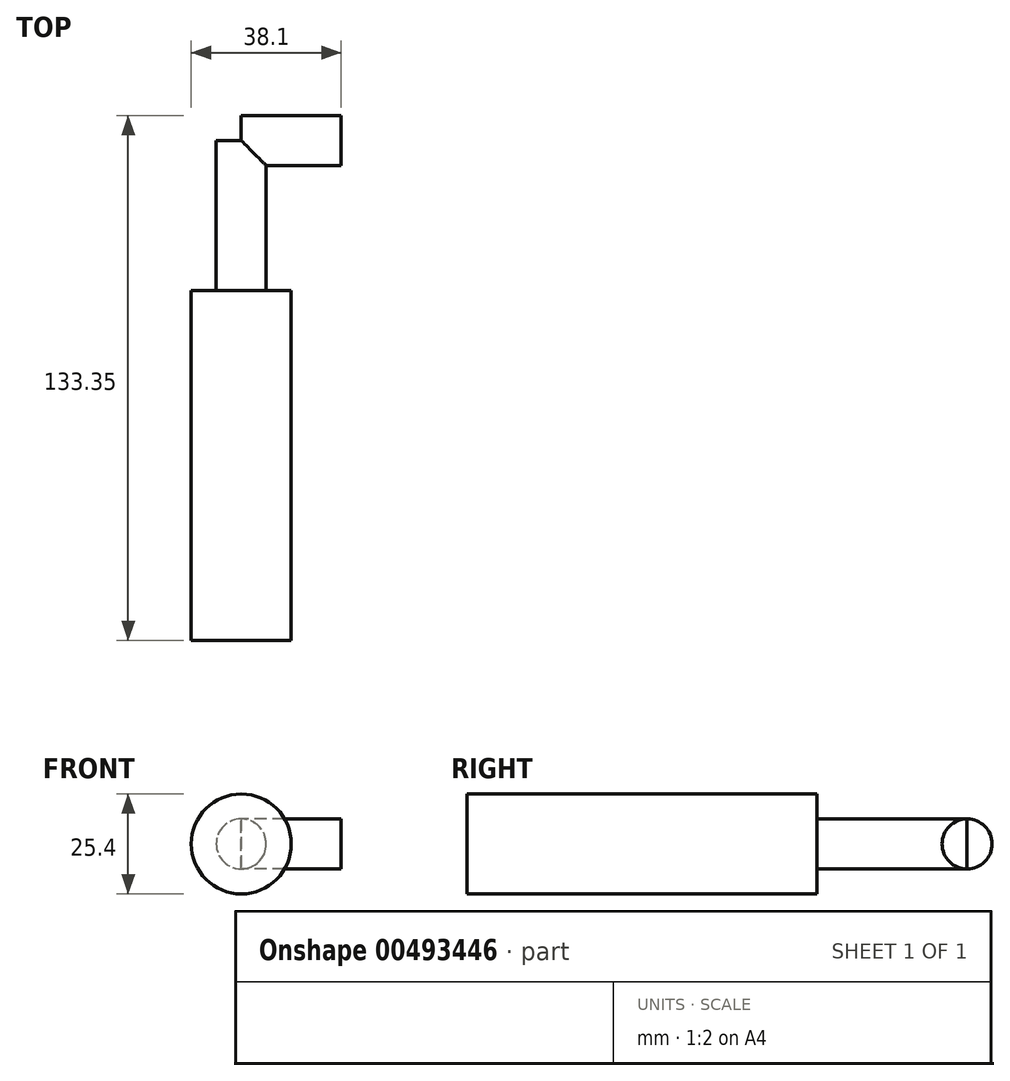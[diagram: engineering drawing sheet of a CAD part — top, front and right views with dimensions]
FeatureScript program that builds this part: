
annotation { "Feature Type Name" : "Feature", "Feature Type Description" : "" }
export const myFeature = defineFeature(function(context is Context, id is Id, definition is map)
    precondition{}
    {
        {
            var Q0;
            Q0=qCreatedBy(makeId("Front.planeOp"),FACE);
            var sketch = newSketch(context, id + "F0", { "sketchPlane" : qUnion([Q0])});
            skCircle(sketch, "E0", {"center": v(0, 0) * mm, "radius": 12.7 * mm});
            skSolve(sketch);
        }
        {
            var Q0;
            Q0=makeQuery(id+"F0.imprint","IMPRINT",FACE,{"disambiguationData":[TD([[makeQuery(id+"F0.imprint","IMPRINT",EDGE,{"derivedFrom":sQuery(id+"F0.wireOp",EDGE,"E0")}),1.0]])]});
            extrude(context, id + "F1", {"entities" : qUnion([Q0]), "oppositeDirection" : true, "depth" : 88.9 * mm});
        }
        {
            var Q0;
            Q0=makeQuery(id+"F1.opExtrude","CAP_FACE",FACE,{"disambiguationData":[OSD([sQuery(id+"F0.wireOp",EDGE,"E0")])],"isStart":false});
            var sketch = newSketch(context, id + "F2", { "sketchPlane" : qUnion([Q0])});
            skCircle(sketch, "E1", {"center": v(0, 0) * mm, "radius": 6.35 * mm});
            skSolve(sketch);
        }
        {
            var Q0;
            Q0=makeQuery(id+"F2.imprint","IMPRINT",FACE,{"disambiguationData":[TD([[makeQuery(id+"F2.imprint","IMPRINT",EDGE,{"derivedFrom":sQuery(id+"F2.wireOp",EDGE,"E1")}),1.0]])]});
            extrude(context, id + "F3", {"entities" : qUnion([Q0]), "operationType" : NewBodyOperationType.ADD, "depth" : 38.1 * mm});
        }
        {
            var Q0;
            Q0=qCreatedBy(makeId("Right.planeOp"),FACE);
            var sketch = newSketch(context, id + "F4", { "sketchPlane" : qUnion([Q0])});
            skCircle(sketch, "E2", {"center": v(127, 0) * mm, "radius": 6.35 * mm});
            skSolve(sketch);
        }
        {
            var Q0;
            Q0=makeQuery(id+"F4.imprint","IMPRINT",FACE,{"disambiguationData":[TD([[makeQuery(id+"F4.imprint","IMPRINT",EDGE,{"derivedFrom":sQuery(id+"F4.wireOp",EDGE,"E2")}),1.0]])]});
            extrude(context, id + "F5", {"entities" : qUnion([Q0]), "operationType" : NewBodyOperationType.ADD, "depth" : 25.4 * mm});
        }
    });
